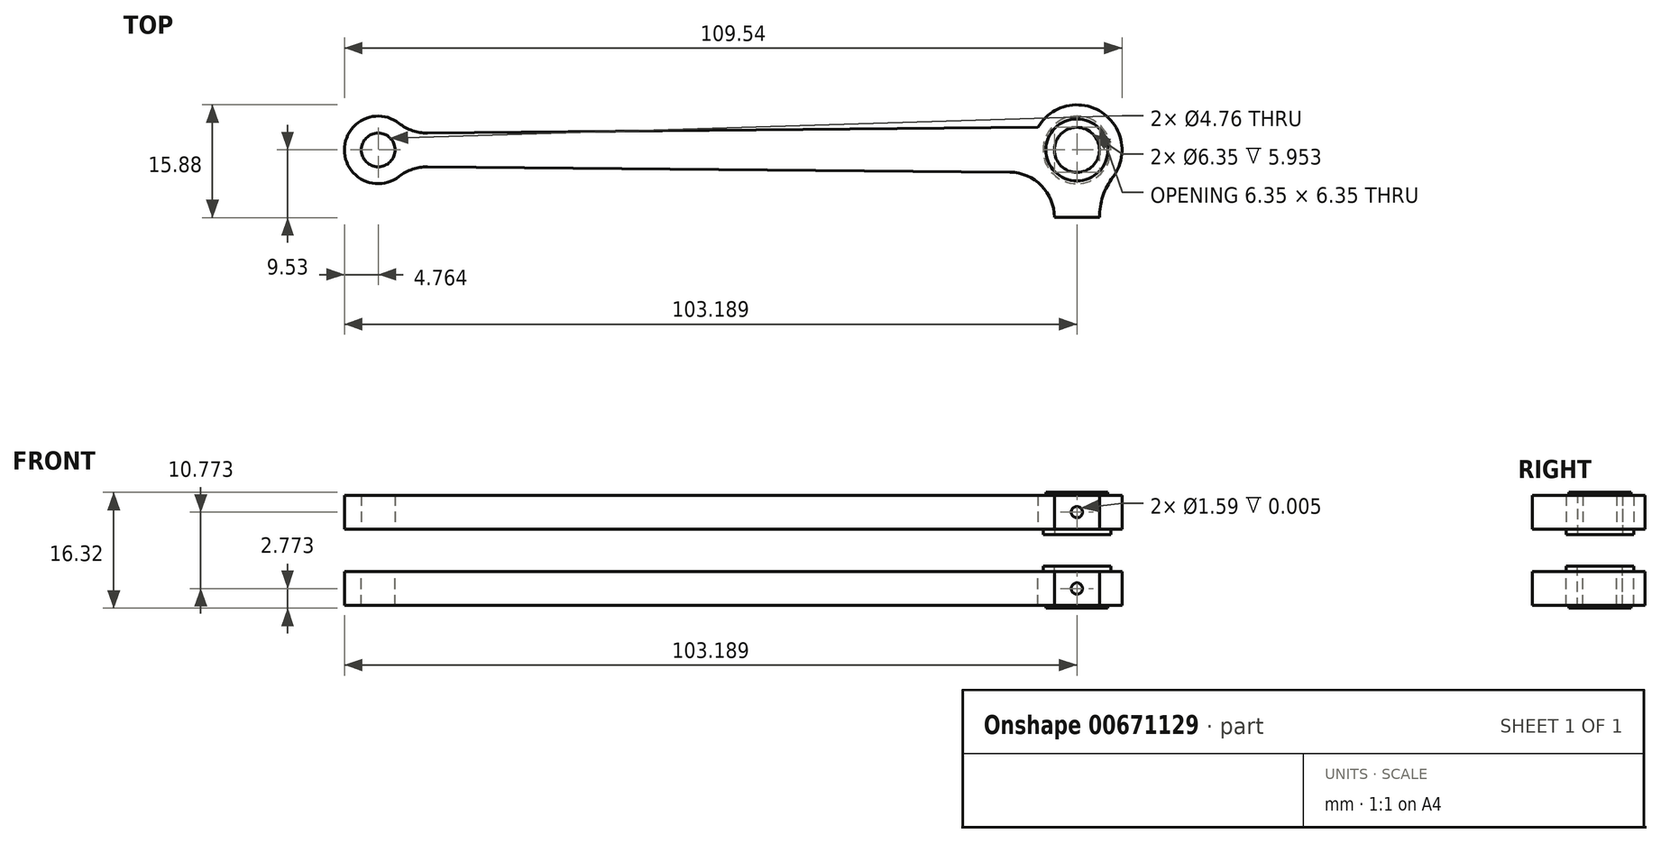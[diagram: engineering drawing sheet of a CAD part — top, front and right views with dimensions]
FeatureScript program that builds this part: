
annotation { "Feature Type Name" : "Feature", "Feature Type Description" : "" }
export const myFeature = defineFeature(function(context is Context, id is Id, definition is map)
    precondition{}
    {
        {
            var Q0;
            Q0=qCreatedBy(makeId("Front.planeOp"),FACE);
            var sketch = newSketch(context, id + "F0", { "sketchPlane" : qUnion([Q0])});
            skLineSegment(sketch, "E0", {"start": v(-31.85, 7.77) * mm, "end": v(77.69, 7.77) * mm});
            skLineSegment(sketch, "E1", {"start": v(77.69, 7.77) * mm, "end": v(77.69, 3) * mm});
            skLineSegment(sketch, "E2", {"start": v(77.69, 3) * mm, "end": v(-31.85, 3) * mm});
            skLineSegment(sketch, "E3", {"start": v(-31.85, 3) * mm, "end": v(-31.85, 7.77) * mm});
            skSolve(sketch);
        }
        {
            var Q0;
            Q0=qSketchRegion(id+"F0",true);
            extrude(context, id + "F1", {"entities" : qUnion([Q0]), "depth" : 15.88 * mm});
        }
        {
            var Q0;
            Q0=makeQuery(id+"F1.opExtrude","SWEPT_FACE",FACE,{"disambiguationData":[OSD([sQuery(id+"F0.wireOp",EDGE,"E2")])]});
            var sketch = newSketch(context, id + "F2", { "sketchPlane" : qUnion([Q0])});
            skLineSegment(sketch, "E4", {"start": v(-27.09, 15.88) * mm, "end": v(-27.09, 0) * mm});
            skLineSegment(sketch, "E5", {"start": v(-31.85, 6.35) * mm, "end": v(77.69, 6.35) * mm});
            skCircle(sketch, "E6", {"center": v(-27.09, 6.35) * mm, "radius": 4.76 * mm});
            skLineSegment(sketch, "E7", {"start": v(71.34, 15.88) * mm, "end": v(71.34, 0) * mm});
            skCircle(sketch, "E8", {"center": v(71.34, 6.35) * mm, "radius": 6.35 * mm});
            skLineSegment(sketch, "E9", {"start": v(-20.15, 8.73) * mm, "end": v(-20.15, 3.97) * mm});
            skLineSegment(sketch, "E10", {"start": v(61.52, 9.53) * mm, "end": v(61.52, 3.18) * mm});
            skLineSegment(sketch, "E11", {"start": v(-20.15, 3.97) * mm, "end": v(65.84, 3.18) * mm});
            skLineSegment(sketch, "E12", {"start": v(-20.15, 8.73) * mm, "end": v(65.84, 9.52) * mm});
            skArc(sketch, "E13", {"start": v(61.87, 9.49) * mm, "mid": v(66.34, 11.38) * mm, "end": v(68.16, 15.88) * mm});
            skArc(sketch, "E14", {"start": v(74.51, 15.87) * mm, "mid": v(75, 12.86) * mm, "end": v(76.42, 10.16) * mm});
            skArc(sketch, "E15", {"start": v(67.12, 1.6) * mm, "mid": v(65.2, 2.78) * mm, "end": v(62.97, 3.2) * mm});
            skArc(sketch, "E16", {"start": v(-24.14, 10.1) * mm, "mid": v(-22.26, 9.07) * mm, "end": v(-20.15, 8.73) * mm});
            skArc(sketch, "E17", {"start": v(-20.15, 3.97) * mm, "mid": v(-22.26, 3.63) * mm, "end": v(-24.14, 2.6) * mm});
            skSolve(sketch);
        }
        {
            var Q0;
            {var subQ3=sQuery(id+"F2.wireOp",EDGE,"E15");Q0=makeQuery(id+"F2.imprint","IMPRINT",FACE,{"disambiguationData":[TD([[makeQuery(id+"F2.imprint","IMPRINT",EDGE,{"derivedFrom":subQ3}),-1.0]])]});}
            var Q1;
            {var subQ0=sQuery(id+"F2.wireOp",EDGE,"E13");Q1=makeQuery(id+"F2.imprint","IMPRINT",FACE,{"disambiguationData":[TD([[makeQuery(id+"F2.imprint","IMPRINT",EDGE,{"derivedFrom":subQ0}),1.0]])]});}
            var Q2;
            {var subQ10=sQuery(id+"F2.wireOp",EDGE,"E15");Q2=makeQuery(id+"F2.imprint","IMPRINT",FACE,{"disambiguationData":[TD([[makeQuery(id+"F2.imprint","IMPRINT",EDGE,{"derivedFrom":subQ10}),1.0]])]});}
            var Q3;
            {var subQ0=sQuery(id+"F2.wireOp",EDGE,"E4");var subQ1=sQuery(id+"F0.wireOp",EDGE,"E2");var subQ2=makeQuery(id+"F1.opExtrude","CAP_EDGE",EDGE,{"disambiguationData":[OSD([subQ1])],"isStart":false});var subQ3=makeQuery(id+"F2.imprint","INTERSECT",VERTEX,{"derivedFrom":[subQ2,subQ0]});Q3=makeQuery(id+"F2.imprint","IMPRINT",FACE,{"disambiguationData":[TD([[makeQuery(id+"F2.imprint","IMPRINT",EDGE,{"disambiguationData":[TD([[subQ3,-1.0]])],"derivedFrom":subQ0}),-1.0]])]});}
            var Q4;
            {var subQ0=sQuery(id+"F2.wireOp",EDGE,"E4");var subQ1=sQuery(id+"F0.wireOp",EDGE,"E2");var subQ2=makeQuery(id+"F1.opExtrude","CAP_EDGE",EDGE,{"disambiguationData":[OSD([subQ1])],"isStart":true});var subQ3=makeQuery(id+"F2.imprint","INTERSECT",VERTEX,{"derivedFrom":[subQ2,subQ0]});Q4=makeQuery(id+"F2.imprint","IMPRINT",FACE,{"disambiguationData":[TD([[makeQuery(id+"F2.imprint","IMPRINT",EDGE,{"disambiguationData":[TD([[subQ3,1.0]])],"derivedFrom":subQ0}),-1.0]])]});}
            var Q5;
            {var subQ4=sQuery(id+"F2.wireOp",EDGE,"E14");Q5=makeQuery(id+"F2.imprint","IMPRINT",FACE,{"disambiguationData":[TD([[makeQuery(id+"F2.imprint","IMPRINT",EDGE,{"derivedFrom":subQ4}),1.0]])]});}
            var Q6;
            {var subQ1=sQuery(id+"F0.wireOp",EDGE,"E2");var subQ2=makeQuery(id+"F1.opExtrude","SWEPT_EDGE",EDGE,{"disambiguationData":[OSD([sQuery(id+"F0.wireOp",EDGE,"E1"),subQ1])]});var subQ4=makeQuery(id+"F1.opExtrude","CAP_EDGE",EDGE,{"disambiguationData":[OSD([subQ1])],"isStart":true});var subQ6=makeQuery(id+"F2.imprint","INTERSECT",VERTEX,{"derivedFrom":[subQ2,subQ4]});Q6=makeQuery(id+"F2.imprint","IMPRINT",FACE,{"disambiguationData":[TD([[makeQuery(id+"F2.imprint","IMPRINT",EDGE,{"disambiguationData":[TD([[subQ6,-1.0]])],"derivedFrom":subQ4}),-1.0]])]});}
            extrude(context, id + "F3", {"entities" : qUnion([Q0, Q1, Q2, Q3, Q4, Q5, Q6]), "operationType" : NewBodyOperationType.REMOVE, "oppositeDirection" : true, "depth" : 4.76 * mm});
        }
        {
            var Q0;
            Q0=makeQuery(id+"F1.opExtrude","SWEPT_FACE",FACE,{"disambiguationData":[OSD([sQuery(id+"F0.wireOp",EDGE,"E2")])]});
            var sketch = newSketch(context, id + "F4", { "sketchPlane" : qUnion([Q0])});
            skCircle(sketch, "E18", {"center": v(-27.09, 6.35) * mm, "radius": 2.38 * mm});
            skSolve(sketch);
        }
        {
            var Q0;
            Q0=qSketchRegion(id+"F4",true);
            extrude(context, id + "F5", {"entities" : qUnion([Q0]), "operationType" : NewBodyOperationType.REMOVE, "oppositeDirection" : true, "depth" : 4.76 * mm});
        }
        {
            var Q0;
            Q0=makeQuery(id+"F1.opExtrude","SWEPT_FACE",FACE,{"disambiguationData":[OSD([sQuery(id+"F0.wireOp",EDGE,"E2")])]});
            var sketch = newSketch(context, id + "F6", { "sketchPlane" : qUnion([Q0])});
            skCircle(sketch, "E19", {"center": v(71.34, 6.35) * mm, "radius": 4.76 * mm});
            skSolve(sketch);
        }
        {
            var Q0;
            Q0=qSketchRegion(id+"F6",true);
            extrude(context, id + "F7", {"entities" : qUnion([Q0]), "operationType" : NewBodyOperationType.ADD, "depth" : 0.8 * mm});
        }
        {
            var Q0;
            Q0=makeQuery(id+"F1.opExtrude","SWEPT_FACE",FACE,{"disambiguationData":[OSD([sQuery(id+"F0.wireOp",EDGE,"E0")])]});
            var sketch = newSketch(context, id + "F8", { "sketchPlane" : qUnion([Q0])});
            skCircle(sketch, "E20", {"center": v(71.34, -6.35) * mm, "radius": 4.37 * mm});
            skSolve(sketch);
        }
        {
            var Q0;
            Q0=qSketchRegion(id+"F8",true);
            extrude(context, id + "F9", {"entities" : qUnion([Q0]), "operationType" : NewBodyOperationType.ADD, "depth" : 0.4 * mm});
        }
        {
            var Q0;
            Q0=makeQuery(id+"F7.opExtrude","CAP_FACE",FACE,{"disambiguationData":[OSD([sQuery(id+"F6.wireOp",EDGE,"E19")])],"isStart":false});
            var sketch = newSketch(context, id + "F10", { "sketchPlane" : qUnion([Q0])});
            skCircle(sketch, "E21", {"center": v(71.34, 6.35) * mm, "radius": 3.18 * mm});
            skSolve(sketch);
        }
        {
            var Q0;
            Q0=qSketchRegion(id+"F10",true);
            extrude(context, id + "F11", {"entities" : qUnion([Q0]), "operationType" : NewBodyOperationType.REMOVE, "oppositeDirection" : true, "depth" : 6.35 * mm});
        }
        {
            var Q0;
            Q0=makeQuery(id+"F1.opExtrude","CAP_FACE",FACE,{"disambiguationData":[OSD([sQuery(id+"F0.wireOp",EDGE,"E0"),sQuery(id+"F0.wireOp",EDGE,"E1"),sQuery(id+"F0.wireOp",EDGE,"E2"),sQuery(id+"F0.wireOp",EDGE,"E3")])],"isStart":false});
            var sketch = newSketch(context, id + "F12", { "sketchPlane" : qUnion([Q0])});
            skPoint(sketch, "E22", {"position": v(71.34, 5.39) * mm});
            skCircle(sketch, "E23", {"center": v(71.34, 5.39) * mm, "radius": 0.8 * mm});
            skSolve(sketch);
        }
        {
            var Q0;
            Q0=qSketchRegion(id+"F12",true);
            extrude(context, id + "F13", {"entities" : qUnion([Q0]), "operationType" : NewBodyOperationType.REMOVE, "oppositeDirection" : true, "depth" : 1 / 203.2 * mm});
        }
        {
            var Q0;
            Q0=qCreatedBy(makeId("Top.planeOp"),FACE);
            var sketch = newSketch(context, id + "F14", { "sketchPlane" : qUnion([Q0])});
            skLineSegment(sketch, "E24.bottom", {"start": v(0, -21.3) * mm, "end": v(57.42, -21.3) * mm});
            skLineSegment(sketch, "E24.top", {"start": v(0, 6.79) * mm, "end": v(57.42, 6.79) * mm});
            skLineSegment(sketch, "E24.left", {"start": v(0, -21.3) * mm, "end": v(0, 6.79) * mm});
            skLineSegment(sketch, "E24.right", {"start": v(57.42, -21.3) * mm, "end": v(57.42, 6.79) * mm});
            skSolve(sketch);
        }
        {
            var Q0;
            Q0=makeQuery(id+"F1.opExtrude","SWEPT_BODY",BODY,{"disambiguationData":[OSD([sQuery(id+"F0.wireOp",EDGE,"E0"),sQuery(id+"F0.wireOp",EDGE,"E1"),sQuery(id+"F0.wireOp",EDGE,"E2"),sQuery(id+"F0.wireOp",EDGE,"E3")])]});
            var Q1;
            Q1=makeQuery(id+"F14.imprint","IMPRINT",FACE,{"disambiguationData":[TD([[makeQuery(id+"F14.imprint","IMPRINT",EDGE,{"derivedFrom":sQuery(id+"F14.wireOp",EDGE,"E24.bottom")}),1.0]])]});
            mirror(context, id + "F15", {"entities" : qUnion([Q0]), "mirrorPlane" : qUnion([Q1])});
        }
    });
